# Revit family: agtatec_Record_SldngDrset_CLEAN-K1_Standalone_Glass
name_source: partatom
category: Doors
revit_build: Autodesk Revit Architecture 2014 (Build: 20130308_1515(x64)
units: mm (PartAtom-declared; Revit-internal decimal feet)

## types (2) — shared parameters
AccessoryOptions = contact manufacturer
AlternativeDoorsetGlazing = Noise protection, radiation protection, smoke- and fire protection
AntiFingerTrapRequirement = No
Assembly Code = B2030300
BIMObjectName = agtatec_Record_SlidingDoorset_CLEAN-K1_Generic
BreakoutFacility = 0
Capacity = <>
ClearanceZones = No
Colour = customer specific
Configuration = 1
Construction Type = Automatic Sliding Door
Description = Automatic Sliding Door
DoorIncluded = Yes
DoorSeal = rubber
DoorsetFasteners = screws
DoorsetOperation = automatic, manual
DurationUnit = year
ElectronicLock = No
Finish = Powder coated, Anodized, customer specific
FireExit = No
FrameColourOptions = all RAL, customer specific
FrameFinish = part of glazing spec
FrameFinishOptions = Powder coated, Anodized, Clad in stainless steel, etc.
FrameMaterial = aluminum, stainless steel, HPL
FrameProfile = aluminum
FrameSeal = Yes
Function = Exterior
GlassLayers = 1
GlassThickness1 = 0
GlassThickness2 = 0
GlassType = customer specific
HandicapAccessible = Yes
HasDrive = Yes
IfcExportAs = IfcDoorStyle
IfcExportType = Door
IsExternal = No
IssueDate = (leave empty)
LeafColourOptions = customer specific
ManufacturerName = Record
ManufacturerURL = www.kos-tueren.de
Material = wood, stainless steel, aluminum, HPL
Model = record CLEAN basic linear slider single leaf
ModelReference = depends on the configuration
NBSDescription = Sliding Doorset
Name = SldngDrset_CLEAN-K1_Generic_Record
NominalHeight = 0.00 mm
NominalLength = 0.00 mm
NominalWidth = 0.00 mm
OpenDoor = No
Opening = 0.00 mm
OpeningMechanism = automatic, manual
OperatingTemperature = -15° to +50°C
Operation = Automatic
PanelGlass = agtatec_Record_Glass
PassageWidthOptions = Depends on diameter, Opening Angle is 69.4° (-70 mm)
ProductInformation = www.agta-record.com
ReferenceStandard = EN16005, DIN 18650, etc.
ReplacementCost = depends on the configuration and door type
Rubber = agtatec_Record_Rubber
SafetyDevices = Fully compliant with EN16005, Safety buffers, Presence sensors, etc.
SelfClosing = Yes
ServiceLifeDuration = 10-15 years
Shape = rectangular
SideStrip = Yes
SideStripWidth = 150.00 mm
SmokeStop = No
Thickness = 0.00 mm
ThresholdRequired = Yes
URL = www.agta-record.com
Uniclass2 = Ss_25_30_20_77
Version = Version 1.0
WarrantyDescription = Depends on country
WarrantyDurationLabour = Depends on country
WarrantyDurationParts = Depends on country
WarrantyGuarantorLabour = Local door manufacturer
WarrantyGuarantorParts = Local door manufacturer
Weight = Depends on configuration and size
Window = Yes
WithinStandardSizes = Yes
zero-valued in all types: Cost, ThermalTransmittance

## per-type parameters (varying)
- CLEAN K1: DimensionUnfinished=1240.00 mm; Frames=agtatec_Record_Aluminium; FreePassage=1075.00 mm; Handle=agtatec_Record_Aluminium; Handles=Yes; Height=2405.00 mm; HeightCentreFlushMountedSocket=2325.00 mm; HeightOfUnfinishedState=2125.00 mm; HeightToTopOfTravellingMechanismCovering=2405.00 mm; InsideFrameHeight=2100.00 mm; InsideFrameWidth=1200.00 mm; OpeningHeight=2100.00 mm; OpeningWidth=1200.00 mm; PanelFill=agtatec_Record_White; PanelWidth=1260.00 mm; Rough Height=2470.00 mm; Rough Width=2455.00 mm; Sensor=agtatec_Record_Aluminium; SideStripMaterial=agtatec_Record_Aluminium; TravellingMechanismCoveringWidth=2455.00 mm; Width=2455.00 mm; WindowHeight=600.00 mm; WindowOpeningHeight=600.00 mm; WindowOpeningWidth=600.00 mm; WindowSillHeight=1200.00 mm; WindowWidth=600.00 mm
- Clean K1 - GlassPanel: DimensionUnfinished=1440.00 mm; Frames=agtatec_Record_StainlessSteel; FreePassage=1275.00 mm; Handle=agtatec_Record_StainlessSteel; Handles=No; Height=2605.00 mm; HeightCentreFlushMountedSocket=2525.00 mm; HeightOfUnfinishedState=2325.00 mm; HeightToTopOfTravellingMechanismCovering=2605.00 mm; InsideFrameHeight=2300.00 mm; InsideFrameWidth=1400.00 mm; OpeningHeight=2300.00 mm; OpeningWidth=1400.00 mm; PanelFill=agtatec_Record_StainlessSteel; PanelWidth=1460.00 mm; Rough Height=2670.00 mm; Rough Width=2855.00 mm; Sensor=agtatec_Record_StainlessSteel; SideStripMaterial=agtatec_Record_StainlessSteel; TravellingMechanismCoveringWidth=2855.00 mm; Width=2855.00 mm; WindowHeight=2170.00 mm; WindowOpeningHeight=2170.00 mm; WindowOpeningWidth=1220.00 mm; WindowSillHeight=120.00 mm; WindowWidth=1220.00 mm

## geometry (parser evidence)
native form markers: Blend x4, Sweep x4
no freeform markers — native parametric forms only
